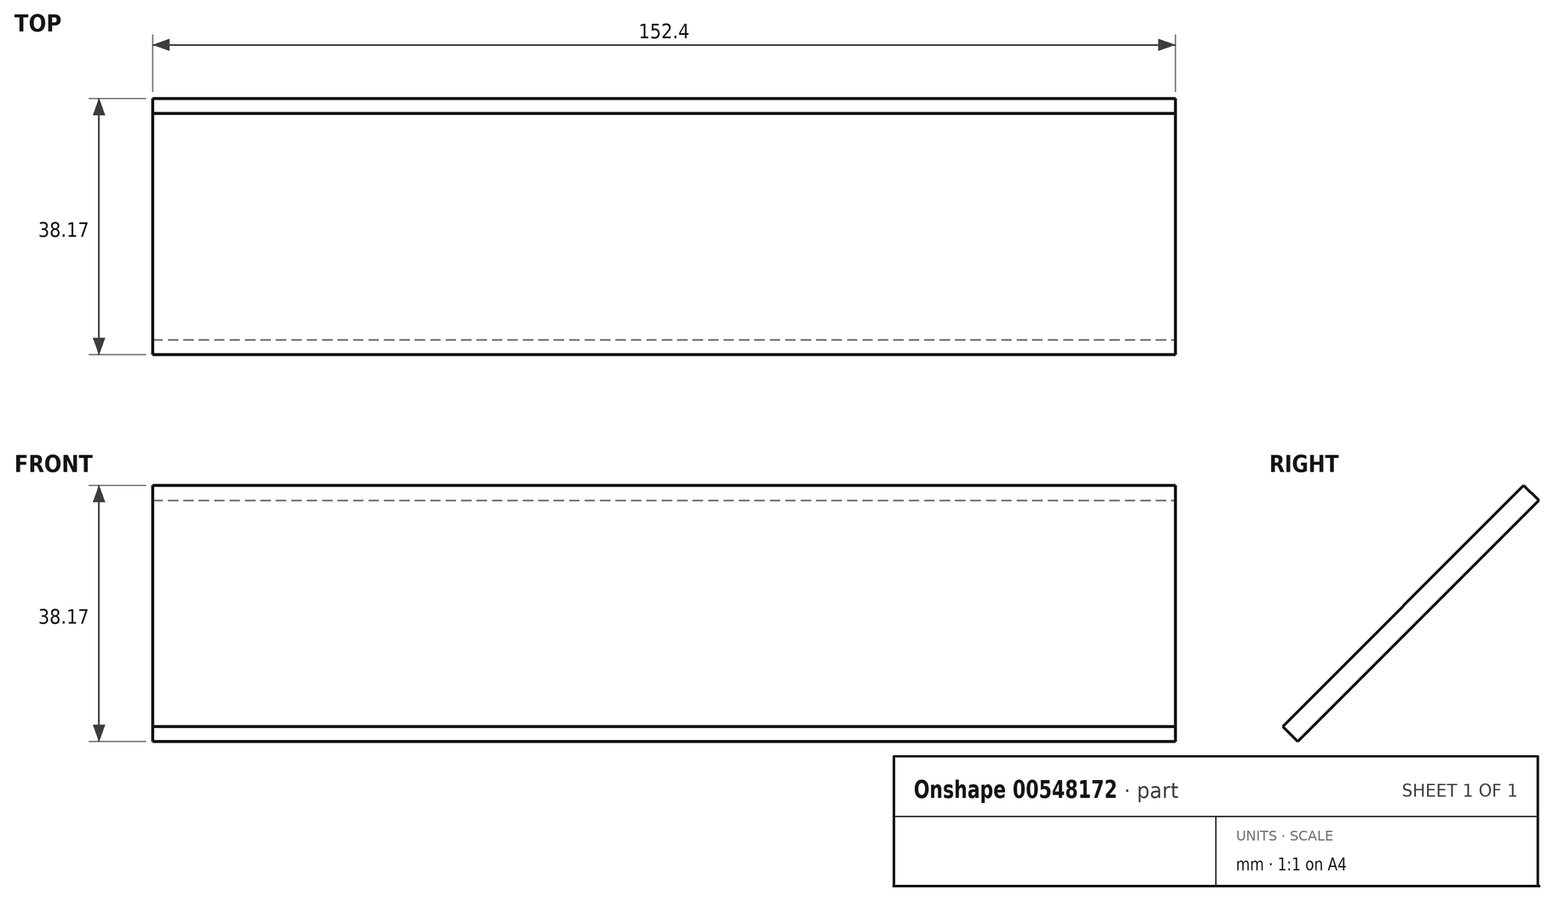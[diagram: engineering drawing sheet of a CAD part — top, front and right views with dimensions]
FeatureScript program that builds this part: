
annotation { "Feature Type Name" : "Feature", "Feature Type Description" : "" }
export const myFeature = defineFeature(function(context is Context, id is Id, definition is map)
    precondition{}
    {
        {
            var Q0;
            Q0=qCreatedBy(makeId("Top.planeOp"),FACE);
            var Q1;
            Q1=qCreatedBy(makeId("Front.planeOp"),FACE);
            cPlane(context, id + "F0", {"entities" : qUnion([Q0, Q1]), "cplaneType" : CPlaneType.MID_PLANE, "offset" : 25.4 * mm, "flipAlignment" : true, "width" : 152.4 * mm, "height" : 152.4 * mm});
        }
        {
            var Q0;
            Q0=qCreatedBy(id+"F0.planeOp",FACE);
            var sketch = newSketch(context, id + "F1", { "sketchPlane" : qUnion([Q0])});
            skLineSegment(sketch, "E0.bottom", {"start": v(-76.2, 50.8) * mm, "end": v(76.2, 50.8) * mm});
            skLineSegment(sketch, "E0.top", {"start": v(-76.2, 0) * mm, "end": v(76.2, 0) * mm});
            skLineSegment(sketch, "E0.left", {"start": v(-76.2, 50.8) * mm, "end": v(-76.2, 0) * mm});
            skLineSegment(sketch, "E0.right", {"start": v(76.2, 50.8) * mm, "end": v(76.2, 0) * mm});
            skSolve(sketch);
        }
        {
            var Q0;
            Q0 = qSketchRegion(id + "F1", true);
            extrude(context, id + "F2", {"entities" : qUnion([Q0]), "depth" : 3.17 * mm, "offsetDistance" : 25.4 * mm});
        }
        {
            var Q0;
            Q0=makeQuery(id+"F2.opExtrude","SWEPT_FACE",FACE,{"disambiguationData":[OSD([sQuery(id+"F1.wireOp",EDGE,"E0.right")])]});
            var sketch = newSketch(context, id + "F3", { "sketchPlane" : qUnion([Q0])});
            skPoint(sketch, "E1", {"position": v(3.37, 5.61) * mm});
            skSolve(sketch);
        }
        {
            var Q0;
            Q0=sQuery(id+"F3.wireOp",VERTEX,"E1");
            var Q1;
            Q1=makeQuery(id+"F2.opExtrude","SWEPT_BODY",BODY,{"disambiguationData":[OSD([sQuery(id+"F1.wireOp",EDGE,"E0.bottom"),sQuery(id+"F1.wireOp",EDGE,"E0.top"),sQuery(id+"F1.wireOp",EDGE,"E0.left"),sQuery(id+"F1.wireOp",EDGE,"E0.right")])]});
            hole(context, id + "F4", {"style" : HoleStyle.SIMPLE, "endStyle" : HoleEndStyle.BLIND, "standardTappedOrClearance" : lookupTablePath({ "standard" : "ANSI", "engagement" : "75%", "pitch" : "56 tpi", "size" : "#2", "type" : "Tapped" }), "standardBlindInLast" : lookupTablePath({ "standard" : "ANSI", "engagement" : "75%", "pitch" : "56 tpi", "size" : "#2", "type" : "Tapped" }), "holeDiameter" : 1.78 * mm, "showTappedDepth" : true, "holeDepth" : 12.25 * mm, "isTappedThrough" : true, "tappedDepth" : 9.52 * mm, "tapClearance" : 6, "locations" : qUnion([Q0]), "scope" : qUnion([Q1]), "majorDiameter" : 2.18 * mm});
        }
        {
            var Q0;
            Q0=makeQuery(id+"F2.opExtrude","SWEPT_BODY",BODY,{"disambiguationData":[OSD([sQuery(id+"F1.wireOp",EDGE,"E0.bottom"),sQuery(id+"F1.wireOp",EDGE,"E0.top"),sQuery(id+"F1.wireOp",EDGE,"E0.left"),sQuery(id+"F1.wireOp",EDGE,"E0.right")])]});
            var Q1;
            Q1=qCreatedBy(makeId("Right.planeOp"),FACE);
            mirror(context, id + "F5", {"operationType" : NewBodyOperationType.ADD, "entities" : qUnion([Q0]), "mirrorPlane" : qUnion([Q1])});
        }
    });
